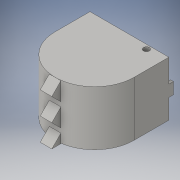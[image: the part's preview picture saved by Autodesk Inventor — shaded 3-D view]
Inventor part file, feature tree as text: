
AUTODESK INVENTOR PART (.ipt)
format: ipt  version: 2016 (Build 200138000, 138)  size: 225,792 bytes
history: native  units: in
note: dims shown in document units (in); Inventor stores cm internally (conversion verified against a paired STEP export)
features: sketch x10, reference x10, extrude x9, plane x1
ambient origin geometry x8: Origin, YZ Plane, XZ Plane, XY Plane, X Axis, Y Axis, Z Axis, Center Point
bodies: Solid1 (feature_tree)
feature tree (30):
  extrude  "Extrusion1"  Depth=1.5in TaperAngle=0.0deg
  extrude  "Extrusion2"  Depth=0.1969in TaperAngle=0.0deg
  extrude  "Extrusion3"  [1 undecoded]
  extrude  "Extrusion4"  Depth=0.3937in
  plane  "Work Plane1"
  sketch  "Sketch5"  dims[d12=1.9685in d14=0.9774in d15=0.3937in d17=1.0in d19=0.5in d20=0.0in]
  extrude  "Extrusion5"  Depth=0.5in TaperAngle=0.0deg
  extrude  "Extrusion6"  Depth=2.0in TaperAngle=0.0deg
  extrude  "Extrusion7"  Depth=16.0in TaperAngle=0.0deg
  extrude  "Extrusion8"  [1 undecoded]
  extrude  "Extrusion9"  [1 undecoded]
  sketch  "Sketch1"  dims[d0=0.1969in d1=1.5in d2=0.0in]
  reference  "Reference1"
  sketch  "Sketch2"  dims[d3=4.6969in d4=0.0in d5=0.1969in d6=0.0in]
  sketch  "Sketch3"  dims[d7=0.1969in d8=0.0in d9=-1.697in]
  sketch  "Sketch4"  dims[d10=0.7874in d11=0.3937in]
  reference  "Reference2"
  sketch  "Sketch6"  dims[d21=0.197in d22=0.0in d23=2.0in d24=0.0in]
  sketch  "Sketch8"  dims[d25=2.0in d26=0.0in d27=16.0in d28=0.0in]
  reference  "Reference3"
  reference  "Reference5"
  reference  "Reference6"
  reference  "Reference7"
  reference  "Reference8"
  reference  "Reference9"
  sketch  "Sketch9"
  reference  "Reference10"
  sketch  "Sketch10"
  reference  "Reference11"
  sketch  "Sketch11"
note: 3 required parameter values undecoded (feature->parameter linkage not recoverable at this tier; creation-order binding heuristic only, values carry confidence <= 0.55)
